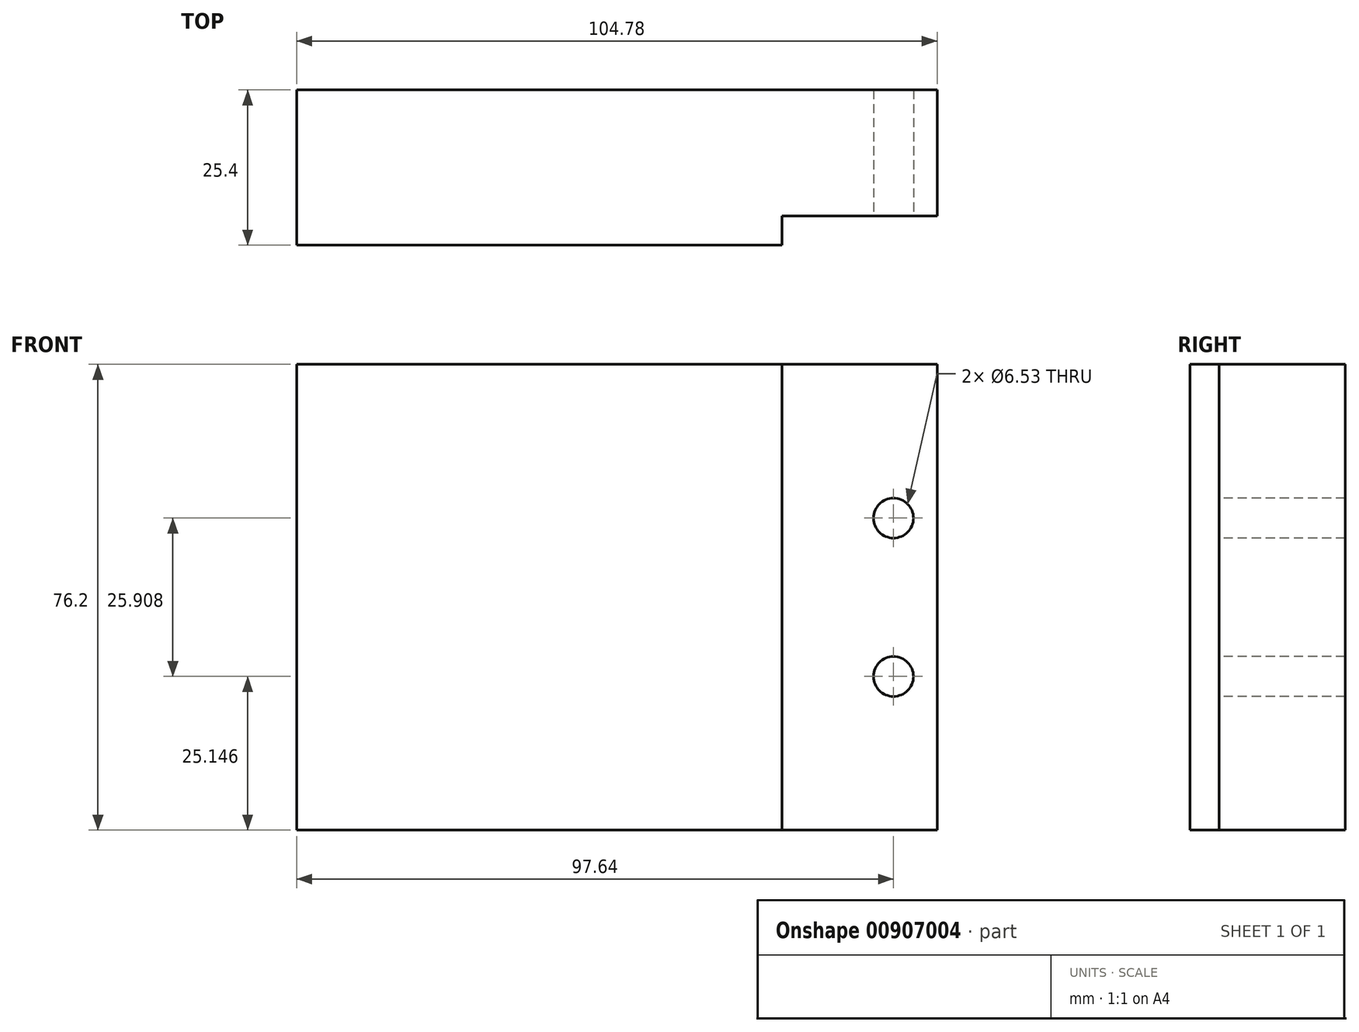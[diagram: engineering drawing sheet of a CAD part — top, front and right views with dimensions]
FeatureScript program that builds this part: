
annotation { "Feature Type Name" : "Feature", "Feature Type Description" : "" }
export const myFeature = defineFeature(function(context is Context, id is Id, definition is map)
    precondition{}
    {
        {
            var Q0;
            Q0=qCreatedBy(makeId("Front.planeOp"),FACE);
            var sketch = newSketch(context, id + "F0", { "sketchPlane" : qUnion([Q0])});
            skLineSegment(sketch, "E0.bottom", {"start": v(52.39, 38.1) * mm, "end": v(-52.39, 38.1) * mm});
            skLineSegment(sketch, "E0.top", {"start": v(52.39, -38.1) * mm, "end": v(-52.39, -38.1) * mm});
            skLineSegment(sketch, "E0.left", {"start": v(52.39, 38.1) * mm, "end": v(52.39, -38.1) * mm});
            skLineSegment(sketch, "E0.right", {"start": v(-52.39, 38.1) * mm, "end": v(-52.39, -38.1) * mm});
            skPoint(sketch, "E0.middle", {"position": v(0, 0) * mm});
            skSolve(sketch);
        }
        {
            var Q0;
            Q0=makeQuery(id+"F0.imprint","IMPRINT",FACE,{"disambiguationData":[TD([[makeQuery(id+"F0.imprint","IMPRINT",EDGE,{"derivedFrom":sQuery(id+"F0.wireOp",EDGE,"E0.bottom")}),1.0]])]});
            extrude(context, id + "F1", {"entities" : qUnion([Q0]), "depth" : 25.4 * mm, "offsetDistance" : 25.4 * mm});
        }
        {
            var Q0;
            Q0=makeQuery(id+"F1.opExtrude","CAP_FACE",FACE,{"disambiguationData":[OSD([sQuery(id+"F0.wireOp",EDGE,"E0.bottom"),sQuery(id+"F0.wireOp",EDGE,"E0.top"),sQuery(id+"F0.wireOp",EDGE,"E0.left"),sQuery(id+"F0.wireOp",EDGE,"E0.right")])],"isStart":false});
            var sketch = newSketch(context, id + "F2", { "sketchPlane" : qUnion([Q0])});
            skLineSegment(sketch, "E1.bottom", {"start": v(52.39, 38.1) * mm, "end": v(26.99, 38.1) * mm});
            skLineSegment(sketch, "E1.top", {"start": v(52.39, -38.1) * mm, "end": v(26.99, -38.1) * mm});
            skLineSegment(sketch, "E1.left", {"start": v(52.39, 38.1) * mm, "end": v(52.39, -38.1) * mm});
            skLineSegment(sketch, "E1.right", {"start": v(26.99, 38.1) * mm, "end": v(26.99, -38.1) * mm});
            skSolve(sketch);
        }
        {
            var Q0;
            Q0=makeQuery(id+"F2.imprint","IMPRINT",FACE,{"disambiguationData":[TD([[makeQuery(id+"F2.imprint","IMPRINT",EDGE,{"derivedFrom":sQuery(id+"F2.wireOp",EDGE,"E1.bottom")}),1.0]])]});
            extrude(context, id + "F3", {"entities" : qUnion([Q0]), "operationType" : NewBodyOperationType.REMOVE, "oppositeDirection" : true, "depth" : 4.78 * mm, "offsetDistance" : 25.4 * mm});
        }
        {
            var Q0;
            Q0=makeQuery(id+"F3.boolean.opBoolean","COPY",FACE,{"derivedFrom":makeQuery(id+"F3.opExtrude","CAP_FACE",FACE,{"disambiguationData":[OSD([sQuery(id+"F2.wireOp",EDGE,"E1.bottom"),sQuery(id+"F2.wireOp",EDGE,"E1.top"),sQuery(id+"F2.wireOp",EDGE,"E1.left"),sQuery(id+"F2.wireOp",EDGE,"E1.right")])],"isStart":false})});
            var sketch = newSketch(context, id + "F4", { "sketchPlane" : qUnion([Q0])});
            skLineSegment(sketch, "E2", {"start": v(45.25, -12.95) * mm, "end": v(45.25, 12.95) * mm, "construction": true});
            skLineSegment(sketch, "E3", {"start": v(52.39, 0) * mm, "end": v(45.25, 0) * mm, "construction": true});
            skSolve(sketch);
        }
        {
            var Q0;
            Q0=sQuery(id+"F4.wireOp",VERTEX,"E2.start");
            var Q1;
            Q1=sQuery(id+"F4.wireOp",VERTEX,"E2.end");
            var Q2;
            Q2=makeQuery(id+"F1.opExtrude","SWEPT_BODY",BODY,{"disambiguationData":[OSD([sQuery(id+"F0.wireOp",EDGE,"E0.bottom"),sQuery(id+"F0.wireOp",EDGE,"E0.top"),sQuery(id+"F0.wireOp",EDGE,"E0.left"),sQuery(id+"F0.wireOp",EDGE,"E0.right")])]});
            hole(context, id + "F5", {"style" : HoleStyle.SIMPLE, "endStyle" : HoleEndStyle.THROUGH, "standardTappedOrClearance" : lookupTablePath({ "standard" : "ANSI", "engagement" : "75%", "pitch" : "18 tpi", "size" : "5/16", "type" : "Tapped" }), "standardBlindInLast" : lookupTablePath({ "standard" : "ANSI", "fit" : "Free", "engagement" : "75%", "pitch" : "18 tpi", "size" : "5/16", "type" : "Clearance & tapped" }), "holeDiameter" : 6.53 * mm, "majorDiameter" : 7.94 * mm, "showTappedDepth" : true, "isTappedThrough" : true, "tappedDepth" : 12.7 * mm, "tapClearance" : 3, "locations" : qUnion([Q0, Q1]), "scope" : qUnion([Q2])});
        }
    });
